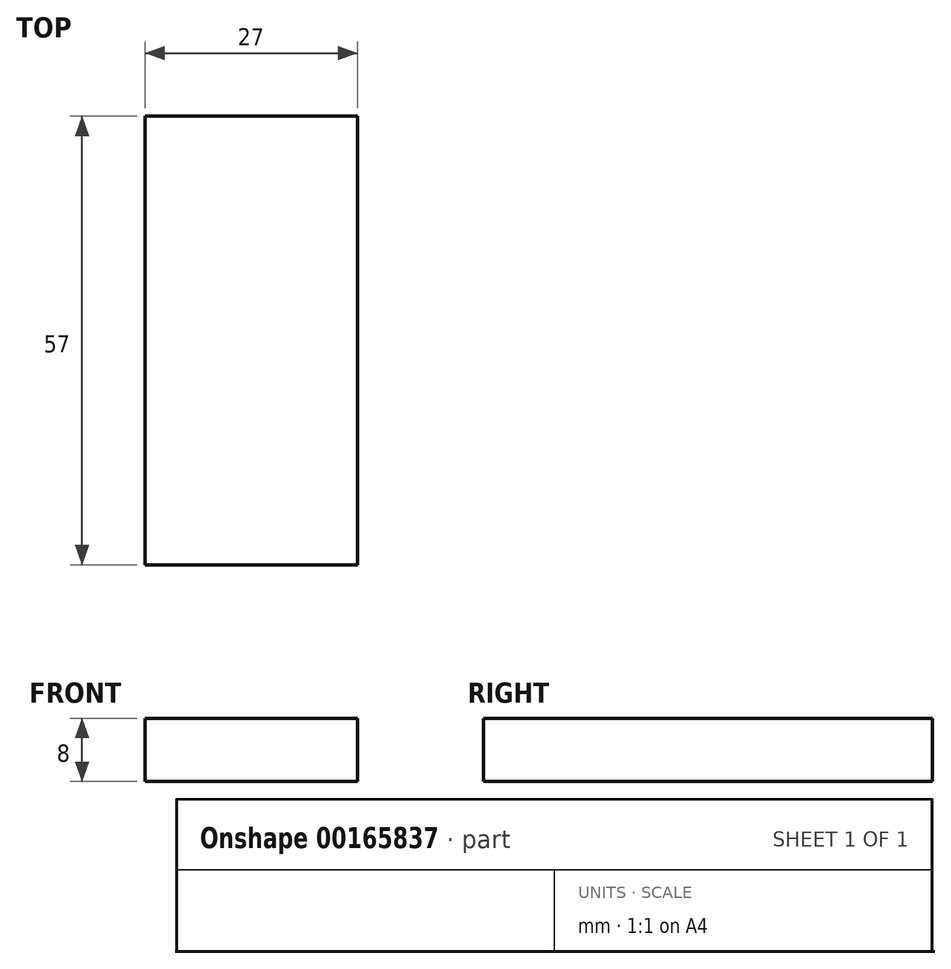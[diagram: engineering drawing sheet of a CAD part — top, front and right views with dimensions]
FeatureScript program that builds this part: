
annotation { "Feature Type Name" : "Feature", "Feature Type Description" : "" }
export const myFeature = defineFeature(function(context is Context, id is Id, definition is map)
    precondition{}
    {
        {
            var Q0;
            Q0=qCreatedBy(makeId("Right.planeOp"),FACE);
            var sketch = newSketch(context, id + "F0", { "sketchPlane" : qUnion([Q0])});
            skLineSegment(sketch, "E0.bottom", {"start": v(28.5, 4) * mm, "end": v(-28.5, 4) * mm});
            skLineSegment(sketch, "E0.top", {"start": v(28.5, -4) * mm, "end": v(-28.5, -4) * mm});
            skLineSegment(sketch, "E0.left", {"start": v(28.5, 4) * mm, "end": v(28.5, -4) * mm});
            skLineSegment(sketch, "E0.right", {"start": v(-28.5, 4) * mm, "end": v(-28.5, -4) * mm});
            skPoint(sketch, "E0.middle", {"position": v(0, 0) * mm});
            skSolve(sketch);
        }
        {
            var Q0;
            Q0 = qSketchRegion(id + "F0", true);
            extrude(context, id + "F1", {"entities" : qUnion([Q0]), "endBound" : BoundingType.SYMMETRIC, "depth" : 27 * mm});
        }
    });
